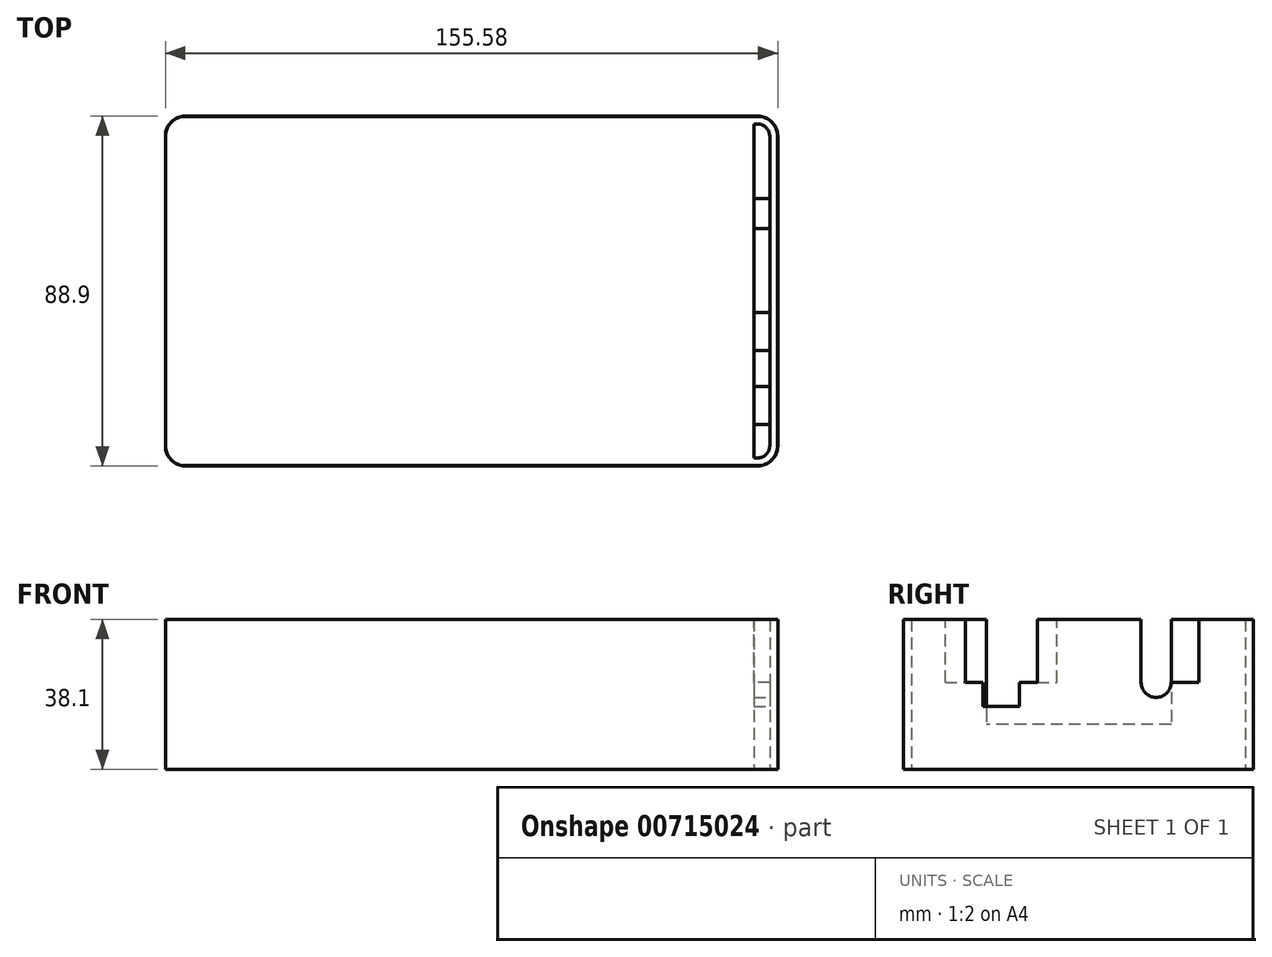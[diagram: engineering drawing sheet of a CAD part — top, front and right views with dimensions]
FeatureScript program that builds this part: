
annotation { "Feature Type Name" : "Feature", "Feature Type Description" : "" }
export const myFeature = defineFeature(function(context is Context, id is Id, definition is map)
    precondition{}
    {
        {
            assignVariable(context, id + "F0", {"name" : "Thickness", "anyValue" : 0.08});
        }
        {
            var Q0;
            Q0=qCreatedBy(makeId("Top.planeOp"),FACE);
            var sketch = newSketch(context, id + "F1", { "sketchPlane" : qUnion([Q0])});
            skLineSegment(sketch, "E0.bottom", {"start": v(-77.79, 44.45) * mm, "end": v(77.79, 44.45) * mm});
            skLineSegment(sketch, "E0.top", {"start": v(-77.79, -44.45) * mm, "end": v(77.79, -44.45) * mm});
            skLineSegment(sketch, "E0.left", {"start": v(-77.79, 44.45) * mm, "end": v(-77.79, -44.45) * mm});
            skLineSegment(sketch, "E0.right", {"start": v(77.79, 44.45) * mm, "end": v(77.79, -44.45) * mm});
            skPoint(sketch, "E0.middle", {"position": v(0, 0) * mm});
            skSolve(sketch);
        }
        {
            var Q0;
            Q0 = qSketchRegion(id + "F1", true);
            extrude(context, id + "F2", {"entities" : qUnion([Q0]), "depth" : 38.1 * mm, "offsetDistance" : 25.4 * mm});
        }
        {
            var Q0;
            Q0=makeQuery(id+"F2.opExtrude","SWEPT_EDGE",EDGE,{"disambiguationData":[OSD([sQuery(id+"F1.wireOp",EDGE,"E0.top"),sQuery(id+"F1.wireOp",EDGE,"E0.right")])]});
            var Q1;
            Q1=makeQuery(id+"F2.opExtrude","SWEPT_EDGE",EDGE,{"disambiguationData":[OSD([sQuery(id+"F1.wireOp",EDGE,"E0.top"),sQuery(id+"F1.wireOp",EDGE,"E0.left")])]});
            var Q2;
            Q2=makeQuery(id+"F2.opExtrude","SWEPT_EDGE",EDGE,{"disambiguationData":[OSD([sQuery(id+"F1.wireOp",EDGE,"E0.bottom"),sQuery(id+"F1.wireOp",EDGE,"E0.right")])]});
            var Q3;
            Q3=makeQuery(id+"F2.opExtrude","SWEPT_EDGE",EDGE,{"disambiguationData":[OSD([sQuery(id+"F1.wireOp",EDGE,"E0.bottom"),sQuery(id+"F1.wireOp",EDGE,"E0.left")])]});
            fillet(context, id + "F3", {"entities" : qUnion([Q0, Q1, Q2, Q3]), "radius" : 5.08 * mm, "tangentPropagation" : true, "allowEdgeOverflow" : false});
        }
        {
            var Q0;
            Q0=makeQuery(id+"F2.opExtrude","CAP_FACE",FACE,{"disambiguationData":[OSD([sQuery(id+"F1.wireOp",EDGE,"E0.bottom"),sQuery(id+"F1.wireOp",EDGE,"E0.top"),sQuery(id+"F1.wireOp",EDGE,"E0.left"),sQuery(id+"F1.wireOp",EDGE,"E0.right")])],"isStart":false});
            shell(context, id + "F4", {"entities" : qUnion([Q0]), "thickness" : (getVariable(context, 'Thickness')) * mm});
        }
        {
            var Q0;
            Q0=makeQuery(id+"F2.opExtrude","SWEPT_FACE",FACE,{"disambiguationData":[OSD([sQuery(id+"F1.wireOp",EDGE,"E0.left")])]});
            var sketch = newSketch(context, id + "F5", { "sketchPlane" : qUnion([Q0])});
            skLineSegment(sketch, "E1.bottom", {"start": v(-23.5, 38.1) * mm, "end": v(23.5, 38.1) * mm});
            skLineSegment(sketch, "E1.top", {"start": v(-23.5, 11.43) * mm, "end": v(23.5, 11.43) * mm});
            skLineSegment(sketch, "E1.left", {"start": v(-23.5, 38.1) * mm, "end": v(-23.5, 11.43) * mm});
            skLineSegment(sketch, "E1.right", {"start": v(23.5, 38.1) * mm, "end": v(23.5, 11.43) * mm});
            skPoint(sketch, "E2", {"position": v(0, 38.1) * mm});
            skSolve(sketch);
        }
        {
            var Q0;
            Q0 = qSketchRegion(id + "F5", true);
            var Q1;
            Q1=makeQuery(id+"F4.opShell","OFFSET_FACE",FACE,{"disambiguationData":[OSD([sQuery(id+"F1.wireOp",EDGE,"E0.left")])]});
            extrude(context, id + "F6", {"entities" : qUnion([Q0]), "operationType" : NewBodyOperationType.REMOVE, "endBound" : BoundingType.UP_TO_SURFACE, "oppositeDirection" : true, "depth" : 25.4 * mm, "endBoundEntityFace" : qUnion([Q1]), "offsetDistance" : 25.4 * mm});
        }
        {
            var Q0;
            Q0=makeQuery(id+"F6.boolean.opBoolean","COPY",FACE,{"derivedFrom":makeQuery(id+"F6.opExtrude","SWEPT_FACE",FACE,{"disambiguationData":[OSD([sQuery(id+"F5.wireOp",EDGE,"E1.top")])]})});
            var sketch = newSketch(context, id + "F7", { "sketchPlane" : qUnion([Q0])});
            skLineSegment(sketch, "E3.bottom", {"start": v(-75.76, 23.5) * mm, "end": v(-77.03, 23.5) * mm});
            skLineSegment(sketch, "E3.top", {"start": v(-75.76, -23.5) * mm, "end": v(-77.03, -23.5) * mm});
            skLineSegment(sketch, "E3.left", {"start": v(-75.76, 23.5) * mm, "end": v(-75.76, -23.5) * mm});
            skLineSegment(sketch, "E3.right", {"start": v(-77.03, 23.5) * mm, "end": v(-77.03, -23.5) * mm});
            skSolve(sketch);
        }
        {
            var Q0;
            Q0 = qSketchRegion(id + "F7", true);
            extrude(context, id + "F8", {"entities" : qUnion([Q0]), "operationType" : NewBodyOperationType.REMOVE, "oppositeDirection" : true, "depth" : 1.27 * mm, "offsetDistance" : 25.4 * mm});
        }
        {
            var Q0;
            Q0=makeQuery(id+"F2.opExtrude","SWEPT_FACE",FACE,{"disambiguationData":[OSD([sQuery(id+"F1.wireOp",EDGE,"E0.right")])]});
            var sketch = newSketch(context, id + "F9", { "sketchPlane" : qUnion([Q0])});
            skLineSegment(sketch, "E4", {"start": v(-28.83, 38.1) * mm, "end": v(-28.83, 22.1) * mm});
            skLineSegment(sketch, "E5", {"start": v(-28.83, 22.1) * mm, "end": v(-24.26, 22.1) * mm});
            skLineSegment(sketch, "E6", {"start": v(-24.26, 22.1) * mm, "end": v(-24.26, 16) * mm});
            skLineSegment(sketch, "E7", {"start": v(-24.26, 16) * mm, "end": v(-15.11, 16) * mm});
            skLineSegment(sketch, "E8", {"start": v(-15.11, 16) * mm, "end": v(-15.11, 22.1) * mm});
            skLineSegment(sketch, "E9", {"start": v(-15.11, 22.1) * mm, "end": v(-10.54, 22.1) * mm});
            skLineSegment(sketch, "E10", {"start": v(-10.54, 22.1) * mm, "end": v(-10.54, 38.1) * mm});
            skLineSegment(sketch, "E11", {"start": v(-10.54, 38.1) * mm, "end": v(-28.83, 38.1) * mm});
            skPoint(sketch, "E12", {"position": v(-19.68, 38.1) * mm});
            skPoint(sketch, "E13", {"position": v(-19.68, 16) * mm});
            skLineSegment(sketch, "E14", {"start": v(-39.37, 38.1) * mm, "end": v(0, 38.1) * mm, "construction": true});
            skLineSegment(sketch, "E15.bottom", {"start": v(15.88, 38.1) * mm, "end": v(23.5, 38.1) * mm});
            skLineSegment(sketch, "E15.top", {"start": v(15.88, 22.1) * mm, "end": v(23.5, 22.1) * mm, "construction": true});
            skLineSegment(sketch, "E15.left", {"start": v(15.88, 38.1) * mm, "end": v(15.88, 22.1) * mm});
            skLineSegment(sketch, "E15.right", {"start": v(23.5, 38.1) * mm, "end": v(23.5, 22.1) * mm});
            skArc(sketch, "E16", {"start": v(15.88, 22.1) * mm, "mid": v(19.69, 18.29) * mm, "end": v(23.5, 22.1) * mm});
            skLineSegment(sketch, "E17", {"start": v(0, 38.1) * mm, "end": v(39.37, 38.1) * mm, "construction": true});
            skPoint(sketch, "E18", {"position": v(19.69, 38.1) * mm});
            skSolve(sketch);
        }
        {
            var Q0;
            Q0=makeQuery(id+"F4.opShell","OFFSET_FACE",FACE,{"disambiguationData":[OSD([sQuery(id+"F1.wireOp",EDGE,"E0.bottom"),sQuery(id+"F1.wireOp",EDGE,"E0.top"),sQuery(id+"F1.wireOp",EDGE,"E0.left"),sQuery(id+"F1.wireOp",EDGE,"E0.right")])]});
            var sketch = newSketch(context, id + "F10", { "sketchPlane" : qUnion([Q0])});
            skLineSegment(sketch, "E19.left", {"start": v(75.76, -39.37) * mm, "end": v(75.76, 39.37) * mm});
            skLineSegment(sketch, "E19.right", {"start": v(71.7, -42.42) * mm, "end": v(71.7, 42.42) * mm});
            skArc(sketch, "E20", {"start": v(72.7, -42.42) * mm, "mid": v(74.86, -41.53) * mm, "end": v(75.76, -39.37) * mm});
            skArc(sketch, "E21", {"start": v(75.76, 39.37) * mm, "mid": v(74.86, 41.53) * mm, "end": v(72.7, 42.42) * mm});
            skLineSegment(sketch, "E22", {"start": v(72.7, 42.42) * mm, "end": v(71.7, 42.42) * mm});
            skLineSegment(sketch, "E23", {"start": v(71.7, -42.42) * mm, "end": v(72.7, -42.42) * mm});
            skSolve(sketch);
        }
        {
            var Q0;
            Q0 = qSketchRegion(id + "F10", true);
            var Q1;
            Q1=makeQuery(id+"F2.opExtrude","CAP_FACE",FACE,{"disambiguationData":[OSD([sQuery(id+"F1.wireOp",EDGE,"E0.bottom"),sQuery(id+"F1.wireOp",EDGE,"E0.top"),sQuery(id+"F1.wireOp",EDGE,"E0.left"),sQuery(id+"F1.wireOp",EDGE,"E0.right")])],"isStart":false});
            extrude(context, id + "F11", {"entities" : qUnion([Q0]), "operationType" : NewBodyOperationType.ADD, "endBound" : BoundingType.UP_TO_SURFACE, "depth" : 25.4 * mm, "endBoundEntityFace" : qUnion([Q1]), "offsetDistance" : 25.4 * mm});
        }
        {
            var Q0;
            Q0 = qSketchRegion(id + "F9", true);
            var Q1;
            Q1=makeQuery(id+"F11.opExtrude","SWEPT_FACE",FACE,{"disambiguationData":[OSD([sQuery(id+"F10.wireOp",EDGE,"E19.right")])]});
            extrude(context, id + "F12", {"entities" : qUnion([Q0]), "operationType" : NewBodyOperationType.REMOVE, "endBound" : BoundingType.UP_TO_SURFACE, "oppositeDirection" : true, "depth" : 25.4 * mm, "endBoundEntityFace" : qUnion([Q1]), "offsetDistance" : 25.4 * mm});
        }
        {
            var Q0;
            {var subQ0=sQuery(id+"F1.wireOp",EDGE,"E0.bottom");var subQ1=sQuery(id+"F1.wireOp",EDGE,"E0.right");var subQ2=sQuery(id+"F1.wireOp",EDGE,"E0.left");var subQ3=sQuery(id+"F1.wireOp",EDGE,"E0.top");Q0=makeQuery(id+"F12.boolean.opBoolean","SPLIT",FACE,{"disambiguationData":[TD([makeQuery(id+"F2.opExtrude","SWEPT_FACE",FACE,{"disambiguationData":[OSD([subQ0])]})])],"derivedFrom":makeQuery(id+"F11.boolean.opBoolean","MERGE",FACE,{"derivedFrom":[makeQuery(id+"F2.opExtrude","CAP_FACE",FACE,{"disambiguationData":[OSD([subQ0,subQ3,subQ2,subQ1])],"isStart":false}),makeQuery(id+"F11.opExtrude","CAP_FACE",FACE,{"disambiguationData":[OSD([subQ0,subQ3,subQ2,subQ1])],"isStart":false})]})});}
            var sketch = newSketch(context, id + "F13", { "sketchPlane" : qUnion([Q0])});
            skLineSegment(sketch, "E24.bottom", {"start": v(77.79, 23.5) * mm, "end": v(76.26, 23.5) * mm});
            skLineSegment(sketch, "E24.top", {"start": v(77.79, 30.6) * mm, "end": v(76.26, 30.6) * mm});
            skLineSegment(sketch, "E24.left", {"start": v(77.79, 23.5) * mm, "end": v(77.79, 30.6) * mm});
            skLineSegment(sketch, "E24.right", {"start": v(76.26, 23.5) * mm, "end": v(76.26, 30.6) * mm});
            skSolve(sketch);
        }
        {
            var Q0;
            Q0 = qSketchRegion(id + "F13", true);
            extrude(context, id + "F14", {"entities" : qUnion([Q0]), "operationType" : NewBodyOperationType.REMOVE, "oppositeDirection" : true, "depth" : 16 * mm, "offsetDistance" : 25.4 * mm});
        }
        {
            var Q0;
            {var subQ0=sQuery(id+"F1.wireOp",EDGE,"E0.right");var subQ1=sQuery(id+"F1.wireOp",EDGE,"E0.top");var subQ2=sQuery(id+"F1.wireOp",EDGE,"E0.left");var subQ3=sQuery(id+"F1.wireOp",EDGE,"E0.bottom");Q0=makeQuery(id+"F12.boolean.opBoolean","SPLIT",FACE,{"disambiguationData":[TD([makeQuery(id+"F2.opExtrude","SWEPT_FACE",FACE,{"disambiguationData":[OSD([subQ1])]})])],"derivedFrom":makeQuery(id+"F11.boolean.opBoolean","MERGE",FACE,{"derivedFrom":[makeQuery(id+"F2.opExtrude","CAP_FACE",FACE,{"disambiguationData":[OSD([subQ3,subQ1,subQ2,subQ0])],"isStart":false}),makeQuery(id+"F11.opExtrude","CAP_FACE",FACE,{"disambiguationData":[OSD([subQ3,subQ1,subQ2,subQ0])],"isStart":false})]})});}
            var sketch = newSketch(context, id + "F15", { "sketchPlane" : qUnion([Q0])});
            skLineSegment(sketch, "E25", {"start": v(77.28, -28.83) * mm, "end": v(77.28, -32.64) * mm});
            skLineSegment(sketch, "E26", {"start": v(77.28, -32.64) * mm, "end": v(76.52, -33.9) * mm});
            skLineSegment(sketch, "E27", {"start": v(76.52, -33.9) * mm, "end": v(71.7, -33.9) * mm});
            skLineSegment(sketch, "E28", {"start": v(71.7, -33.9) * mm, "end": v(71.7, -28.83) * mm});
            skLineSegment(sketch, "E29", {"start": v(71.7, -28.83) * mm, "end": v(77.28, -28.83) * mm});
            skLineSegment(sketch, "E30", {"start": v(77.28, -10.54) * mm, "end": v(77.28, -6.73) * mm});
            skLineSegment(sketch, "E31", {"start": v(77.28, -6.73) * mm, "end": v(76.52, -5.46) * mm});
            skLineSegment(sketch, "E32", {"start": v(76.52, -5.46) * mm, "end": v(71.7, -5.46) * mm});
            skLineSegment(sketch, "E33", {"start": v(71.7, -5.46) * mm, "end": v(71.7, -10.54) * mm});
            skLineSegment(sketch, "E34", {"start": v(71.7, -10.54) * mm, "end": v(77.28, -10.54) * mm});
            skSolve(sketch);
        }
        {
            var Q0;
            Q0 = qSketchRegion(id + "F15", true);
            var Q1;
            Q1=makeQuery(id+"F12.boolean.opBoolean","COPY",FACE,{"derivedFrom":makeQuery(id+"F12.opExtrude","SWEPT_FACE",FACE,{"disambiguationData":[OSD([sQuery(id+"F9.wireOp",EDGE,"E5")])]})});
            extrude(context, id + "F16", {"entities" : qUnion([Q0]), "operationType" : NewBodyOperationType.REMOVE, "endBound" : BoundingType.UP_TO_SURFACE, "oppositeDirection" : true, "depth" : 25.4 * mm, "endBoundEntityFace" : qUnion([Q1]), "offsetDistance" : 25.4 * mm});
        }
    });
